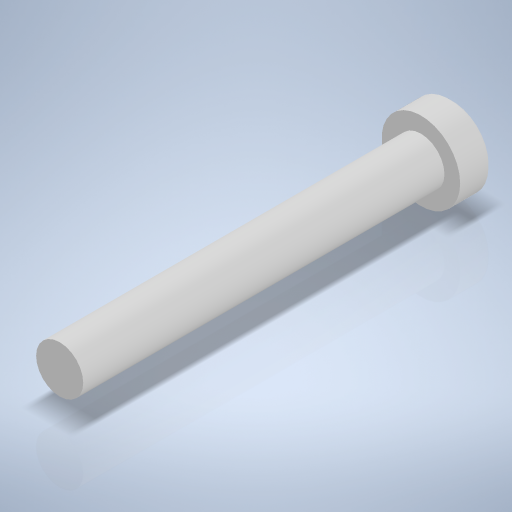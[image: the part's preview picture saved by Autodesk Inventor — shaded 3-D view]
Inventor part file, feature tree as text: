
AUTODESK INVENTOR PART (.ipt)
format: ipt  version: 2024 (Build 280153000, 153)  size: 248,320 bytes
history: native  units: mm
features: revolve x1, chamfer x1, sketch x1
ambient origin geometry x8: Origin, YZ Plane, XZ Plane, XY Plane, X Axis, Y Axis, Z Axis, Center Point
bodies: Volumenkörper1 (feature_tree)
feature tree (3):
  revolve  "Umdrehung1"
  chamfer  "Fasen1"  Distance=2.0mm
  sketch  "Skizze1"  dims[d0=3.0mm d1=2.0mm d2=5.0mm d3=23.0mm d4=90.0deg d5=0.2mm d6=2.0mm d7=45.0deg]
